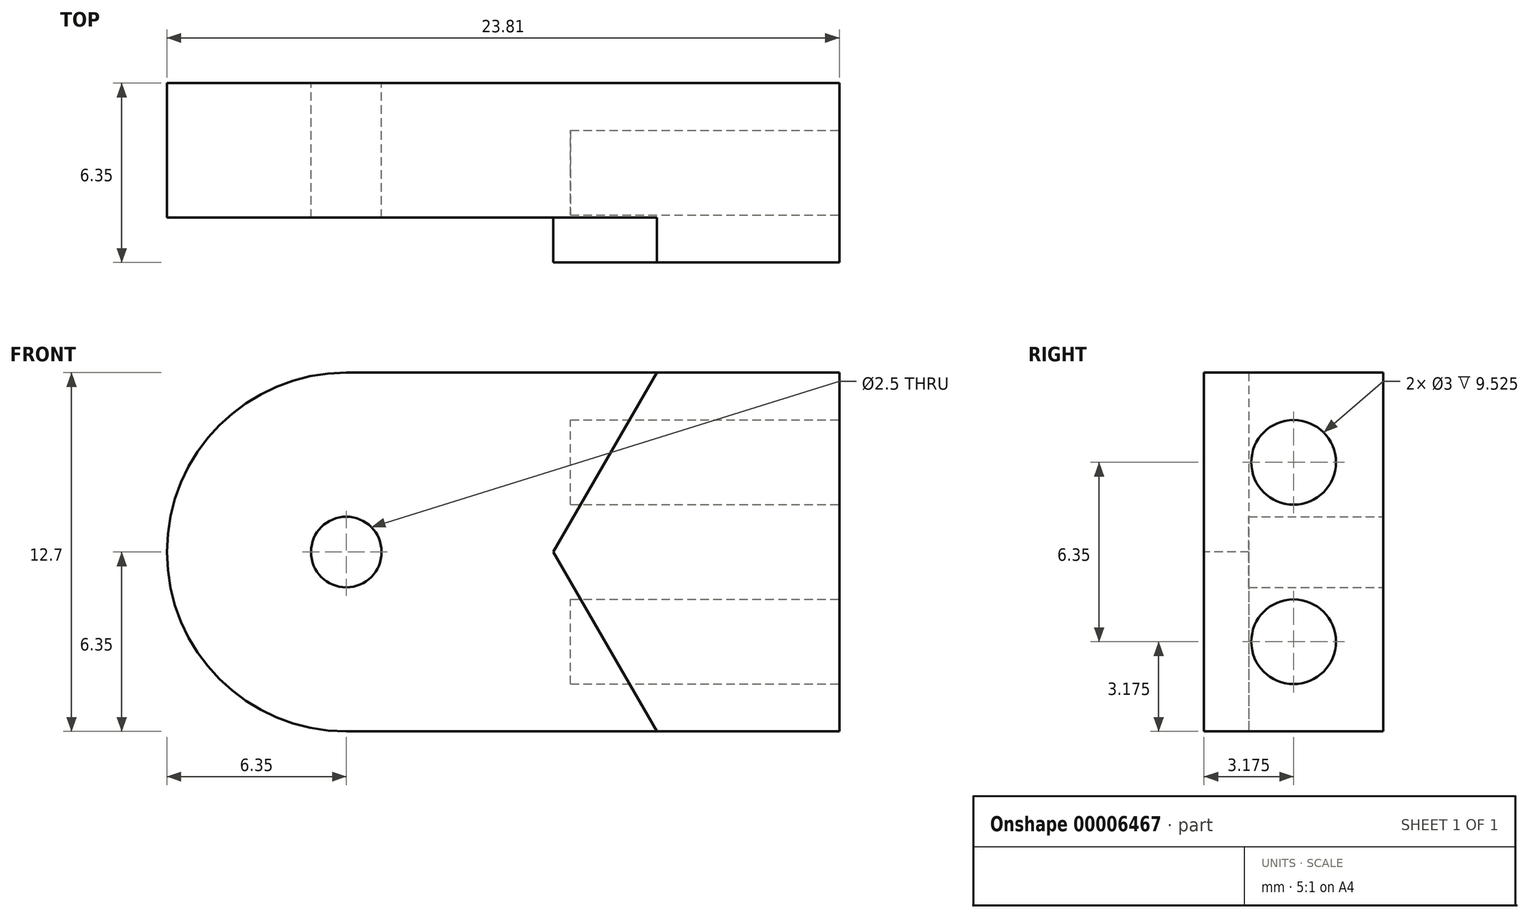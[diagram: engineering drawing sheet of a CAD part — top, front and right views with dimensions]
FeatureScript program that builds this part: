
annotation { "Feature Type Name" : "Feature", "Feature Type Description" : "" }
export const myFeature = defineFeature(function(context is Context, id is Id, definition is map)
    precondition{}
    {
        {
            var Q0;
            Q0=qCreatedBy(makeId("Front.planeOp"),FACE);
            var sketch = newSketch(context, id + "F0", { "sketchPlane" : qUnion([Q0])});
            skLineSegment(sketch, "E0.bottom", {"start": v(0, 0) * mm, "end": v(17.46, 0) * mm});
            skLineSegment(sketch, "E0.top", {"start": v(0, 12.7) * mm, "end": v(17.46, 12.7) * mm});
            skLineSegment(sketch, "E0.left", {"start": v(0, 0) * mm, "end": v(0, 12.7) * mm});
            skLineSegment(sketch, "E0.right", {"start": v(17.46, 0) * mm, "end": v(17.46, 12.7) * mm});
            skArc(sketch, "E1", {"start": v(0, 12.7) * mm, "mid": v(-6.35, 6.35) * mm, "end": v(0, 0) * mm});
            skCircle(sketch, "E2", {"center": v(0, 6.35) * mm, "radius": 7.94 * mm, "construction": true});
            skCircle(sketch, "E3", {"center": v(0, 6.35) * mm, "radius": 1.25 * mm});
            skSolve(sketch);
        }
        {
            var Q0;
            Q0 = qSketchRegion(id + "F0", true);
            extrude(context, id + "F1", {"entities" : qUnion([Q0]), "depth" : 6.35 * mm});
        }
        {
            var Q0;
            Q0=makeQuery(id+"F1.opExtrude","SWEPT_FACE",FACE,{"disambiguationData":[OSD([sQuery(id+"F0.wireOp",EDGE,"E0.right")])]});
            var sketch = newSketch(context, id + "F2", { "sketchPlane" : qUnion([Q0])});
            skCircle(sketch, "E4", {"center": v(-3.18, 9.52) * mm, "radius": 1.5 * mm});
            skCircle(sketch, "E5", {"center": v(-3.18, 3.17) * mm, "radius": 1.5 * mm});
            skLineSegment(sketch, "E6", {"start": v(-3.18, 0) * mm, "end": v(-3.18, 3.17) * mm, "construction": true});
            skLineSegment(sketch, "E7", {"start": v(-3.18, 9.52) * mm, "end": v(-3.18, 12.7) * mm, "construction": true});
            skSolve(sketch);
        }
        {
            var Q0;
            Q0 = qSketchRegion(id + "F2", true);
            extrude(context, id + "F3", {"entities" : qUnion([Q0]), "operationType" : NewBodyOperationType.REMOVE, "oppositeDirection" : true, "depth" : 9.52 * mm});
        }
        {
            var Q0;
            Q0=makeQuery(id+"F1.opExtrude","CAP_FACE",FACE,{"disambiguationData":[OSD([sQuery(id+"F0.wireOp",EDGE,"E0.bottom"),sQuery(id+"F0.wireOp",EDGE,"E0.top"),sQuery(id+"F0.wireOp",EDGE,"E0.right"),sQuery(id+"F0.wireOp",EDGE,"E1"),sQuery(id+"F0.wireOp",EDGE,"E3")])],"isStart":false});
            var sketch = newSketch(context, id + "F4", { "sketchPlane" : qUnion([Q0])});
            skLineSegment(sketch, "E8", {"start": v(11, 12.7) * mm, "end": v(7.33, 6.35) * mm});
            skLineSegment(sketch, "E9", {"start": v(7.33, 6.35) * mm, "end": v(11, 0) * mm});
            skPoint(sketch, "E10", {"position": v(0, 6.35) * mm});
            skLineSegment(sketch, "E11", {"start": v(11, 12.7) * mm, "end": v(-9.92, 14.63) * mm});
            skLineSegment(sketch, "E12", {"start": v(-9.92, 14.63) * mm, "end": v(-4.79, -2.1) * mm});
            skLineSegment(sketch, "E13", {"start": v(-4.79, -2.1) * mm, "end": v(11, 0) * mm});
            skSolve(sketch);
        }
        {
            var Q0;
            Q0 = qSketchRegion(id + "F4", true);
            extrude(context, id + "F5", {"entities" : qUnion([Q0]), "operationType" : NewBodyOperationType.REMOVE, "oppositeDirection" : true, "depth" : 1.59 * mm});
        }
    });
